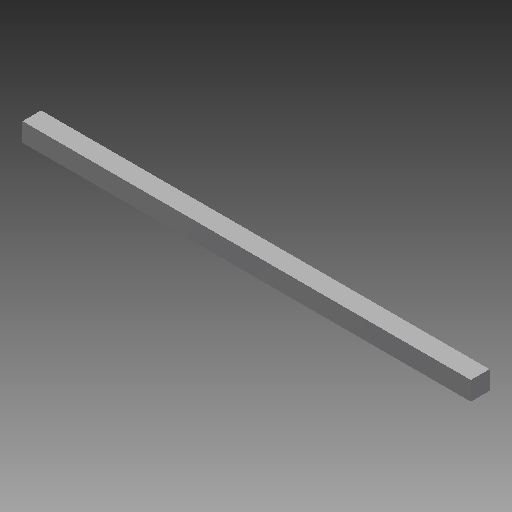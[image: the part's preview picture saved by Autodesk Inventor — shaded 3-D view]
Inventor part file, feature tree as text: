
AUTODESK INVENTOR PART (.ipt)
format: ipt  version: 2017 SP1 (Build 210196100, 196)  size: 100,864 bytes
history: native  units: mm
features: other x5, revolve x1
ambient origin geometry x6: Origin, XZ Plane, XY Plane, X Axis, Y Axis, Z Axis
bodies: Solid1 (feature_tree)
feature tree (6):
  revolve  "Revolution1"  [1 undecoded]
  other  "N-Side1"
  other  "Start Plane"
  other  "Origin point"
  other  "Main Sketch"
  other  "iFeature1:1"
note: 1 required parameter value undecoded (feature->parameter linkage not recoverable at this tier; creation-order binding heuristic only, values carry confidence <= 0.55)
